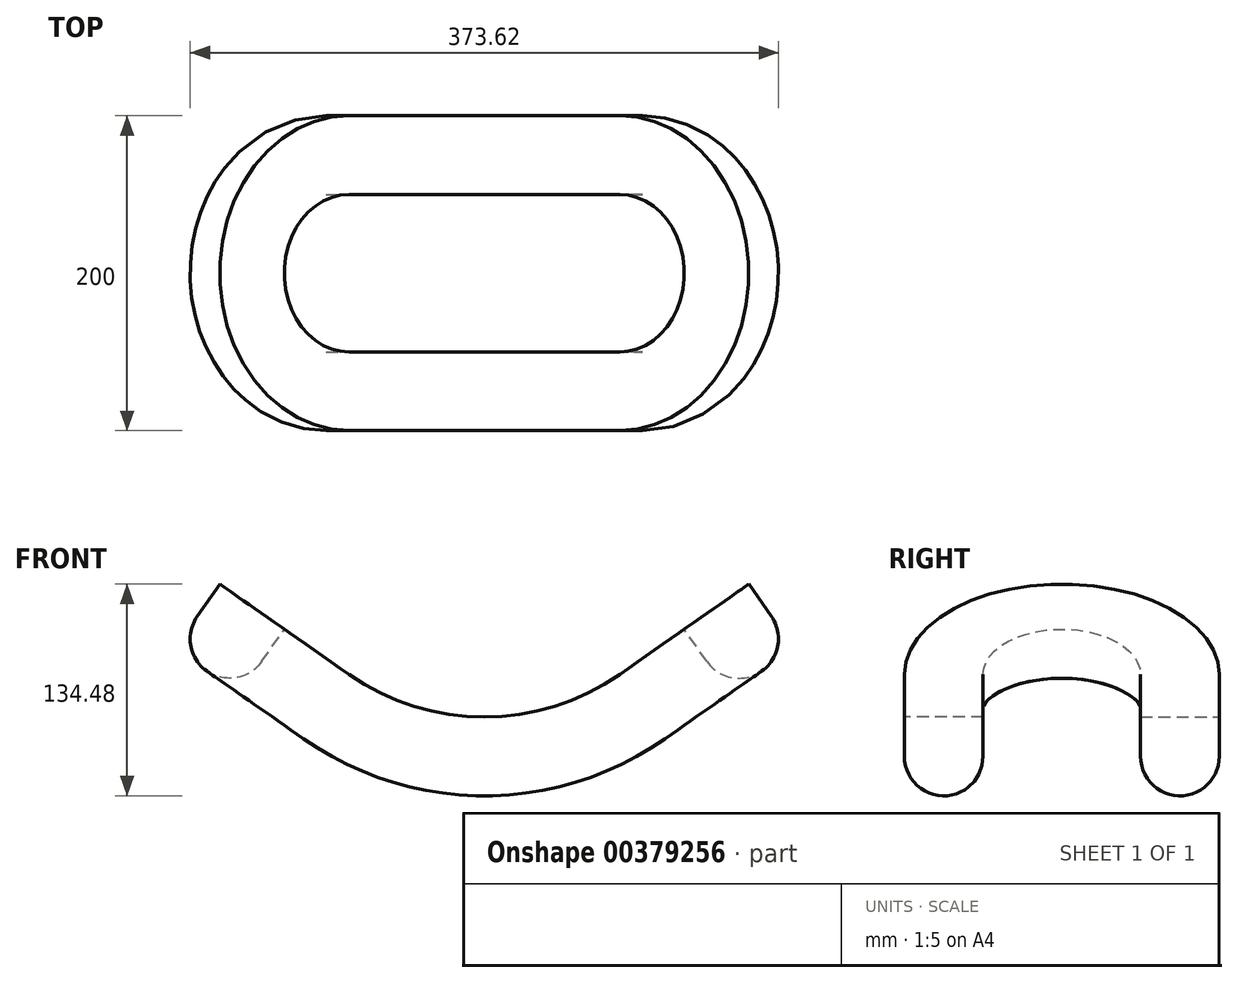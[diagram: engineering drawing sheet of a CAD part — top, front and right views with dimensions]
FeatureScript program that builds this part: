
annotation { "Feature Type Name" : "Feature", "Feature Type Description" : "" }
export const myFeature = defineFeature(function(context is Context, id is Id, definition is map)
    precondition{}
    {
        {
            var Q0;
            Q0=qCreatedBy(makeId("Front.planeOp"),FACE);
            var sketch = newSketch(context, id + "F0", { "sketchPlane" : qUnion([Q0])});
            skArc(sketch, "E0", {"start": v(0, 0) * mm, "mid": v(45.1, 6.94) * mm, "end": v(86.04, 27.13) * mm});
            skLineSegment(sketch, "E1", {"start": v(0, 150) * mm, "end": v(86.04, 27.13) * mm, "construction": true});
            skLineSegment(sketch, "E2", {"start": v(86.04, 27.13) * mm, "end": v(167.95, 84.48) * mm});
            skSolve(sketch);
        }
        {
            var Q0;
            Q0=sQuery(id+"F0.wireOp",EDGE,"E2");
            var Q1;
            Q1=sQuery(id+"F0.wireOp",EDGE,"E0");
            extrude(context, id + "F1", {"bodyType" : ToolBodyType.SURFACE, "surfaceEntities" : qUnion([Q0, Q1]), "depth" : 100 * mm});
        }
        {
            var Q0;
            Q0=makeQuery(id+"F1.opExtrude","SWEPT_FACE",FACE,{"disambiguationData":[OSD([sQuery(id+"F0.wireOp",EDGE,"E2")])]});
            var sketch = newSketch(context, id + "F2", { "sketchPlane" : qUnion([Q0])});
            skArc(sketch, "E3", {"start": v(186.04, 0) * mm, "mid": v(156.75, 70.71) * mm, "end": v(86.04, 100) * mm});
            skSolve(sketch);
        }
        {
            var Q0;
            Q0=qCreatedBy(makeId("Right.planeOp"),FACE);
            var sketch = newSketch(context, id + "F3", { "sketchPlane" : qUnion([Q0])});
            skLineSegment(sketch, "E4.bottom", {"start": v(-50, -25) * mm, "end": v(-100, -25) * mm, "construction": true});
            skLineSegment(sketch, "E4.top", {"start": v(-50, 0) * mm, "end": v(-100, 0) * mm});
            skLineSegment(sketch, "E4.left", {"start": v(-50, -25) * mm, "end": v(-50, 0) * mm});
            skLineSegment(sketch, "E4.right", {"start": v(-100, -25) * mm, "end": v(-100, 0) * mm});
            skArc(sketch, "E5", {"start": v(-50, -25) * mm, "mid": v(-75, -50) * mm, "end": v(-100, -25) * mm});
            skSolve(sketch);
        }
        {
            var Q0;
            Q0=makeQuery(id+"F3.imprint","IMPRINT",FACE,{"disambiguationData":[TD([[makeQuery(id+"F3.imprint","IMPRINT",EDGE,{"derivedFrom":sQuery(id+"F3.wireOp",EDGE,"E4.top")}),1.0]])]});
            var Q1;
            Q1=makeQuery(id+"F1.opExtrude","CAP_EDGE",EDGE,{"disambiguationData":[OSD([sQuery(id+"F0.wireOp",EDGE,"E0")])],"isStart":false});
            var Q2;
            Q2=sQuery(id+"F2.wireOp",EDGE,"E3");
            sweep(context, id + "F4", {"profiles" : qUnion([Q0]), "path" : qUnion([Q1, Q2])});
        }
        {
            var Q0;
            Q0=makeQuery(id+"F4.opSweep","SWEPT_BODY",BODY,{"disambiguationData":[OSD([sQuery(id+"F2.wireOp",EDGE,"E3"),sQuery(id+"F3.wireOp",EDGE,"E4.top"),sQuery(id+"F3.wireOp",EDGE,"E4.left"),sQuery(id+"F3.wireOp",EDGE,"E4.right"),sQuery(id+"F3.wireOp",EDGE,"E5")])]});
            var Q1;
            Q1=qCreatedBy(makeId("Front.planeOp"),FACE);
            mirror(context, id + "F5", {"operationType" : NewBodyOperationType.ADD, "entities" : qUnion([Q0]), "mirrorPlane" : qUnion([Q1])});
        }
        {
            var Q0;
            Q0=makeQuery(id+"F4.opSweep","SWEPT_BODY",BODY,{"disambiguationData":[OSD([sQuery(id+"F2.wireOp",EDGE,"E3"),sQuery(id+"F3.wireOp",EDGE,"E4.top"),sQuery(id+"F3.wireOp",EDGE,"E4.left"),sQuery(id+"F3.wireOp",EDGE,"E4.right"),sQuery(id+"F3.wireOp",EDGE,"E5")])]});
            var Q1;
            Q1=qCreatedBy(makeId("Right.planeOp"),FACE);
            mirror(context, id + "F6", {"operationType" : NewBodyOperationType.ADD, "entities" : qUnion([Q0]), "mirrorPlane" : qUnion([Q1])});
        }
    });
